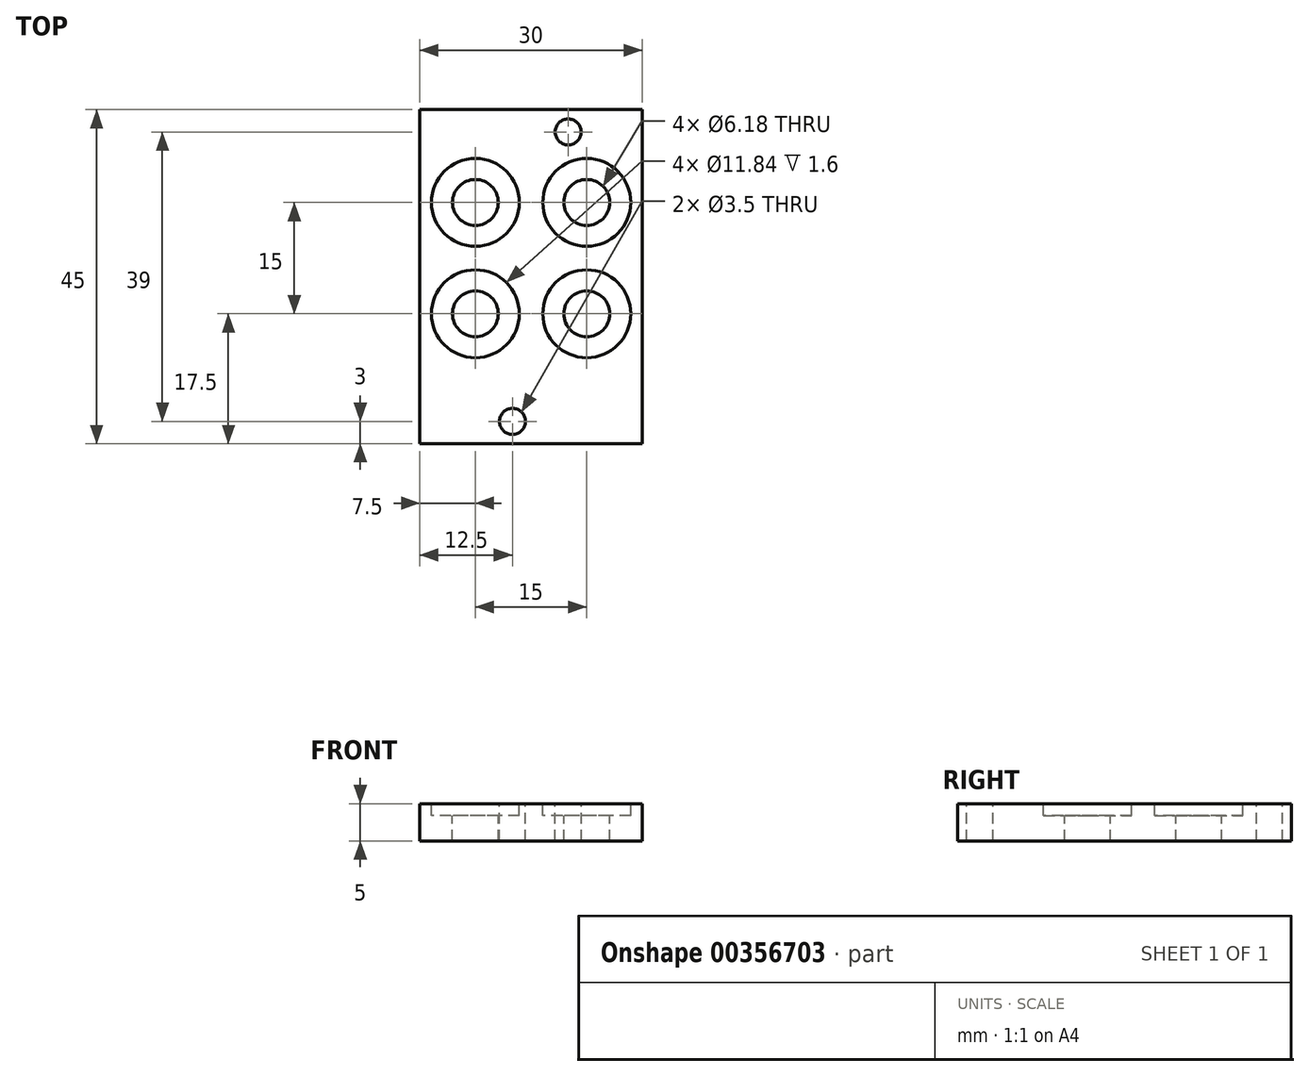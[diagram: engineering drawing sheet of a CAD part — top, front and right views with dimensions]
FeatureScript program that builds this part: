
annotation { "Feature Type Name" : "Feature", "Feature Type Description" : "" }
export const myFeature = defineFeature(function(context is Context, id is Id, definition is map)
    precondition{}
    {
        {
            var Q0;
            Q0=qCreatedBy(makeId("Top.planeOp"),FACE);
            var sketch = newSketch(context, id + "F0", { "sketchPlane" : qUnion([Q0])});
            skLineSegment(sketch, "E0.bottom", {"start": v(-15, 22.5) * mm, "end": v(15, 22.5) * mm});
            skLineSegment(sketch, "E0.top", {"start": v(-15, -22.5) * mm, "end": v(15, -22.5) * mm});
            skLineSegment(sketch, "E0.left", {"start": v(-15, 22.5) * mm, "end": v(-15, -22.5) * mm});
            skLineSegment(sketch, "E0.right", {"start": v(15, 22.5) * mm, "end": v(15, -22.5) * mm});
            skSolve(sketch);
        }
        {
            var Q0;
            Q0=qSketchRegion(id+"F0",true);
            extrude(context, id + "F1", {"entities" : qUnion([Q0]), "depth" : 5 * mm});
        }
        {
            var Q0;
            Q0=makeQuery(id+"F1.opExtrude","CAP_FACE",FACE,{"disambiguationData":[OSD([sQuery(id+"F0.wireOp",EDGE,"E0.bottom"),sQuery(id+"F0.wireOp",EDGE,"E0.top"),sQuery(id+"F0.wireOp",EDGE,"E0.left"),sQuery(id+"F0.wireOp",EDGE,"E0.right")])],"isStart":false});
            var sketch = newSketch(context, id + "F2", { "sketchPlane" : qUnion([Q0])});
            skCircle(sketch, "E1", {"center": v(-7.5, 10) * mm, "radius": 3.09 * mm});
            skCircle(sketch, "E2", {"center": v(-7.5, -5) * mm, "radius": 3.09 * mm});
            skCircle(sketch, "E3", {"center": v(7.5, 10) * mm, "radius": 3.09 * mm});
            skCircle(sketch, "E4", {"center": v(7.5, -5) * mm, "radius": 3.09 * mm});
            skSolve(sketch);
        }
        {
            var Q0;
            Q0=qSketchRegion(id+"F2",true);
            extrude(context, id + "F3", {"entities" : qUnion([Q0]), "operationType" : NewBodyOperationType.REMOVE, "endBound" : BoundingType.UP_TO_NEXT, "oppositeDirection" : true, "depth" : 25 * mm});
        }
        {
            var Q0;
            Q0=makeQuery(id+"F1.opExtrude","CAP_FACE",FACE,{"disambiguationData":[OSD([sQuery(id+"F0.wireOp",EDGE,"E0.bottom"),sQuery(id+"F0.wireOp",EDGE,"E0.top"),sQuery(id+"F0.wireOp",EDGE,"E0.left"),sQuery(id+"F0.wireOp",EDGE,"E0.right")])],"isStart":false});
            var sketch = newSketch(context, id + "F4", { "sketchPlane" : qUnion([Q0])});
            skCircle(sketch, "E5", {"center": v(-7.5, 10) * mm, "radius": 5.92 * mm});
            skCircle(sketch, "E6", {"center": v(7.5, 10) * mm, "radius": 5.92 * mm});
            skCircle(sketch, "E7", {"center": v(7.5, -5) * mm, "radius": 5.92 * mm});
            skCircle(sketch, "E8", {"center": v(-7.5, -5) * mm, "radius": 5.92 * mm});
            skSolve(sketch);
        }
        {
            var Q0;
            Q0=qSketchRegion(id+"F4",true);
            extrude(context, id + "F5", {"entities" : qUnion([Q0]), "operationType" : NewBodyOperationType.REMOVE, "oppositeDirection" : true, "depth" : 1.6 * mm});
        }
        {
            var Q0;
            Q0=makeQuery(id+"F1.opExtrude","CAP_FACE",FACE,{"disambiguationData":[OSD([sQuery(id+"F0.wireOp",EDGE,"E0.bottom"),sQuery(id+"F0.wireOp",EDGE,"E0.top"),sQuery(id+"F0.wireOp",EDGE,"E0.left"),sQuery(id+"F0.wireOp",EDGE,"E0.right")])],"isStart":false});
            var sketch = newSketch(context, id + "F6", { "sketchPlane" : qUnion([Q0])});
            skCircle(sketch, "E9", {"center": v(5, 19.5) * mm, "radius": 1.75 * mm});
            skCircle(sketch, "E10", {"center": v(-2.5, -19.5) * mm, "radius": 1.75 * mm});
            skSolve(sketch);
        }
        {
            var Q0;
            Q0=qSketchRegion(id+"F6",true);
            extrude(context, id + "F7", {"entities" : qUnion([Q0]), "operationType" : NewBodyOperationType.REMOVE, "endBound" : BoundingType.UP_TO_NEXT, "oppositeDirection" : true, "depth" : 25 * mm});
        }
    });
